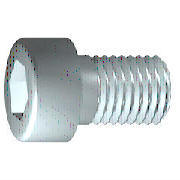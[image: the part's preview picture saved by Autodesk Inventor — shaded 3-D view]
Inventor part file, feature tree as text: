
AUTODESK INVENTOR PART (.ipt)
format: ipt  version: 2019.1 (Build 231200000, 200)  size: 193,024 bytes
history: native  units: mm (DEFAULTED — no unit token found)
features: sketch x2, extrude x1, plane x1, fillet x1
ambient origin geometry x7: Origin, YZ Plane, XY Plane, X Axis, Y Axis, Z Axis, Center Point
bodies: Solid1 (feature_tree), Body (feature_tree)
feature tree (5):
  extrude  "Slot"  Depth=3.0mm
  plane  "Work Plane1"
  fillet  "Fillet2"  Radius=3.0mm
  sketch  "Sketch1"  dims[d1=4.75mm d2=0.306825mm d3=3.0mm]
  sketch  "Sketch2"  dims[d4=1.3mm d5=60.0deg d6=3.0mm d7=3.0mm d8=2.886751mm d9=5.5mm d10=90.0deg d11=10.0mm d12=0.0mm d13=4.75mm d14=0.0mm d15=0.306725mm d16=0.306725mm d17=0.3mm d19=0.0mm d26=6.0mm d27=45.0deg d28=0.0mm d29=0.0mm d30=0.1mm]
